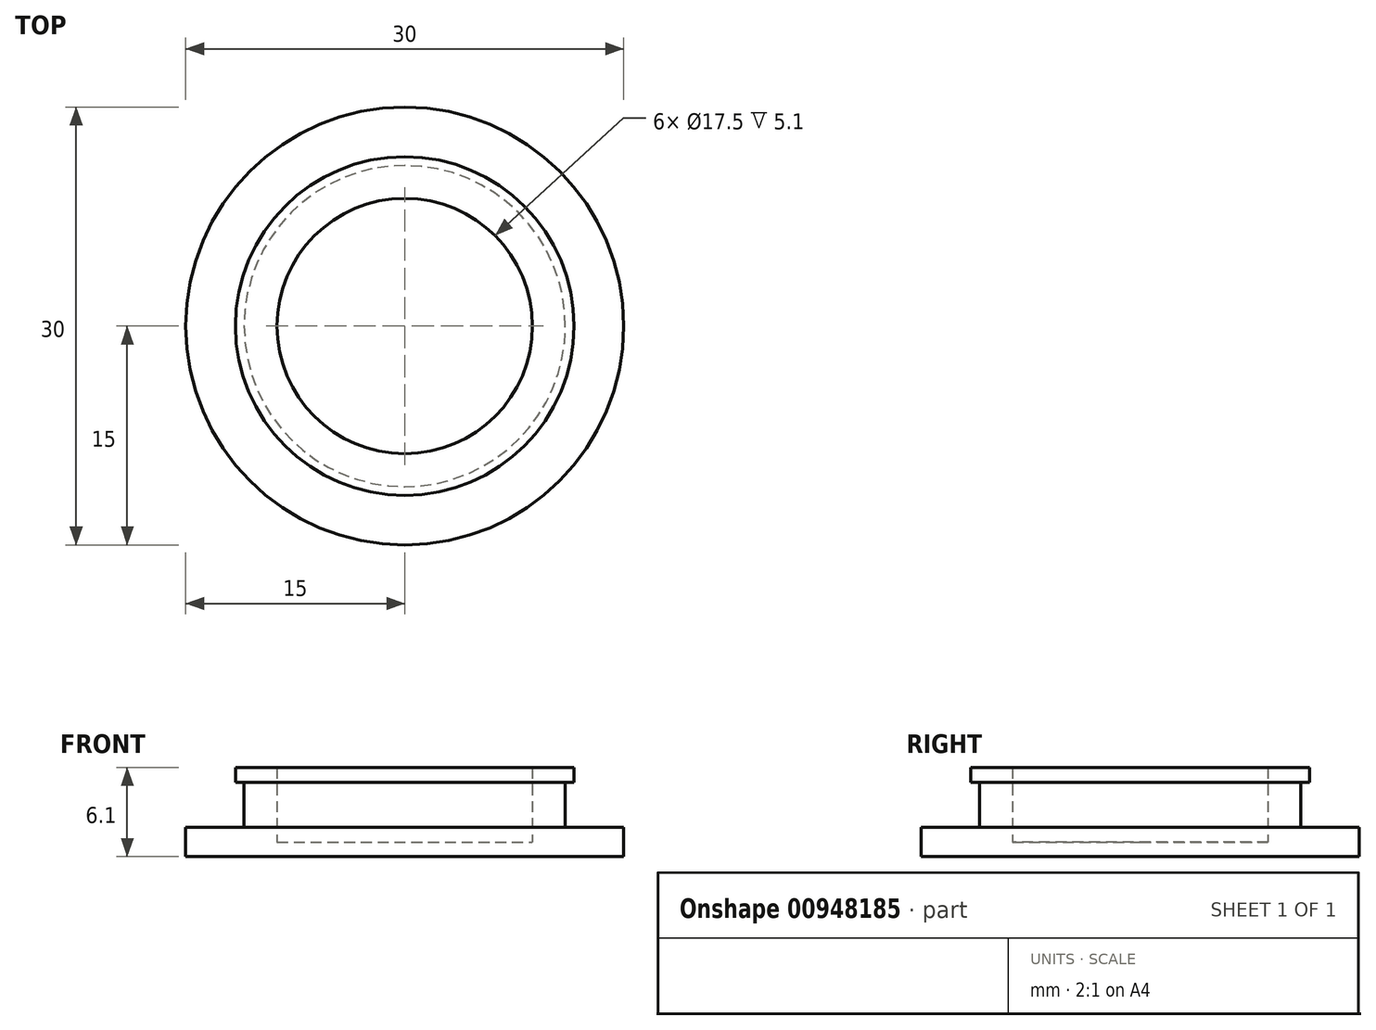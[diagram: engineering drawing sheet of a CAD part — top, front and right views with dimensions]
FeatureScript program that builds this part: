
annotation { "Feature Type Name" : "Feature", "Feature Type Description" : "" }
export const myFeature = defineFeature(function(context is Context, id is Id, definition is map)
    precondition{}
    {
        {
            var Q0;
            Q0=qCreatedBy(makeId("Front.planeOp"),FACE);
            var sketch = newSketch(context, id + "F0", { "sketchPlane" : qUnion([Q0])});
            skLineSegment(sketch, "E0", {"start": v(0, 0) * mm, "end": v(-15, 0) * mm});
            skLineSegment(sketch, "E1", {"start": v(-15, 0) * mm, "end": v(-15, 2) * mm});
            skLineSegment(sketch, "E2", {"start": v(-15, 2) * mm, "end": v(-11, 2) * mm});
            skLineSegment(sketch, "E3", {"start": v(-11, 2) * mm, "end": v(-11, 5.1) * mm});
            skLineSegment(sketch, "E4", {"start": v(-11, 5.1) * mm, "end": v(-11.6, 5.1) * mm});
            skLineSegment(sketch, "E5", {"start": v(-11.6, 5.1) * mm, "end": v(-11.6, 6.1) * mm});
            skLineSegment(sketch, "E6", {"start": v(-11.6, 6.1) * mm, "end": v(-8.75, 6.1) * mm});
            skLineSegment(sketch, "E7", {"start": v(-8.75, 6.1) * mm, "end": v(-8.75, 1) * mm});
            skLineSegment(sketch, "E8", {"start": v(-8.75, 1) * mm, "end": v(0, 1) * mm});
            skLineSegment(sketch, "E9", {"start": v(0, 1) * mm, "end": v(0, 0) * mm});
            skLineSegment(sketch, "E10", {"start": v(0, 1) * mm, "end": v(0, 6.1) * mm, "construction": true});
            skLineSegment(sketch, "E11", {"start": v(0, 6.1) * mm, "end": v(-8.75, 6.1) * mm, "construction": true});
            skSolve(sketch);
        }
        {
            var Q0;
            Q0 = qSketchRegion(id + "F0", true);
            var Q1;
            Q1=sQuery(id+"F0.wireOp",EDGE,"E10");
            revolve(context, id + "F1", {"surfaceOperationType" : NewSurfaceOperationType.NEW, "entities" : qUnion([Q0]), "axis" : qUnion([Q1]), "revolveType" : RevolveType.FULL});
        }
    });
